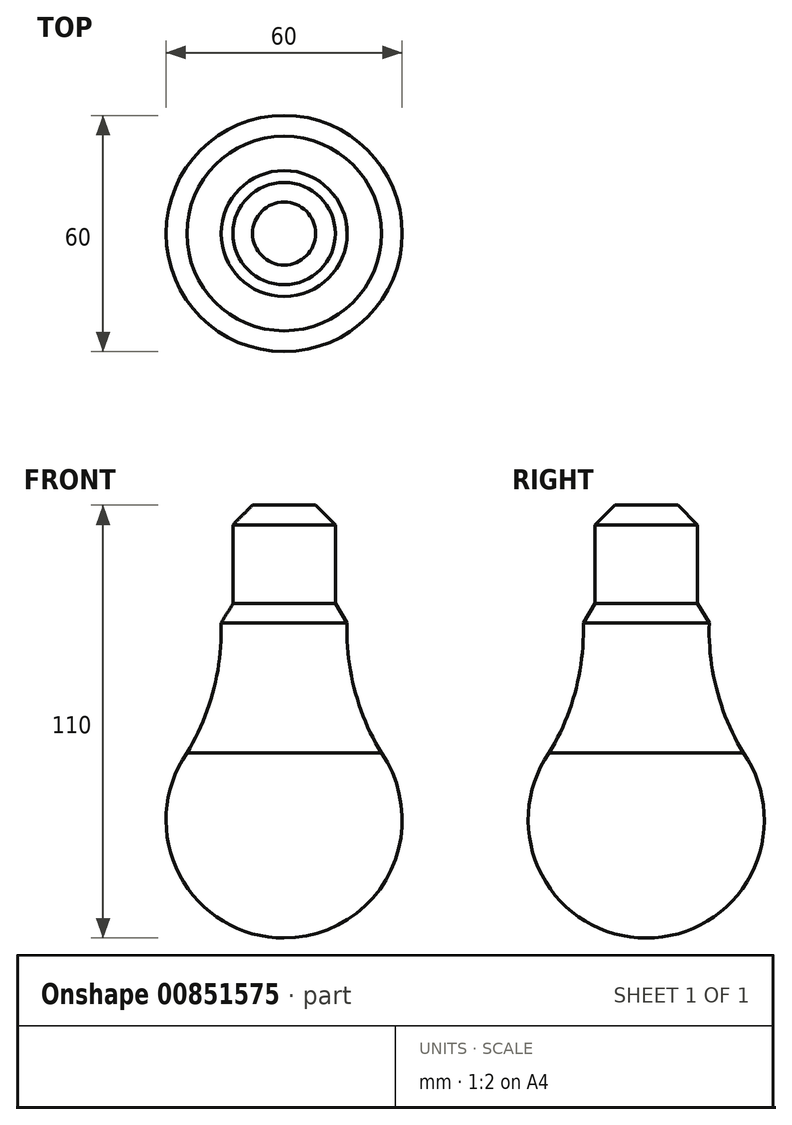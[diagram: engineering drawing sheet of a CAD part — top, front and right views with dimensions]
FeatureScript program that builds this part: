
annotation { "Feature Type Name" : "Feature", "Feature Type Description" : "" }
export const myFeature = defineFeature(function(context is Context, id is Id, definition is map)
    precondition{}
    {
        {
            var Q0;
            Q0=qCreatedBy(makeId("Front.planeOp"),FACE);
            var sketch = newSketch(context, id + "F0", { "sketchPlane" : qUnion([Q0])});
            skLineSegment(sketch, "E0", {"start": v(0, 0) * mm, "end": v(8, 0) * mm});
            skLineSegment(sketch, "E1", {"start": v(8, 0) * mm, "end": v(13, -5) * mm});
            skLineSegment(sketch, "E2", {"start": v(13, -5) * mm, "end": v(13, -25) * mm});
            skLineSegment(sketch, "E3", {"start": v(13, -25) * mm, "end": v(16, -30) * mm});
            skArc(sketch, "E4", {"start": v(0, -110) * mm, "mid": v(26.55, -93.96) * mm, "end": v(24.72, -63) * mm});
            skLineSegment(sketch, "E5", {"start": v(0, -110) * mm, "end": v(0, 0) * mm});
            skArc(sketch, "E6.filletArc", {"start": v(16, -30) * mm, "mid": v(17.96, -47.13) * mm, "end": v(24.72, -63) * mm});
            skSolve(sketch);
        }
        {
            var Q0;
            Q0=qSketchRegion(id+"F0",true);
            var Q1;
            Q1=sQuery(id+"F0.wireOp",EDGE,"E5");
            revolve(context, id + "F1", {"surfaceOperationType" : NewSurfaceOperationType.NEW, "entities" : qUnion([Q0]), "axis" : qUnion([Q1]), "revolveType" : RevolveType.FULL});
        }
    });
